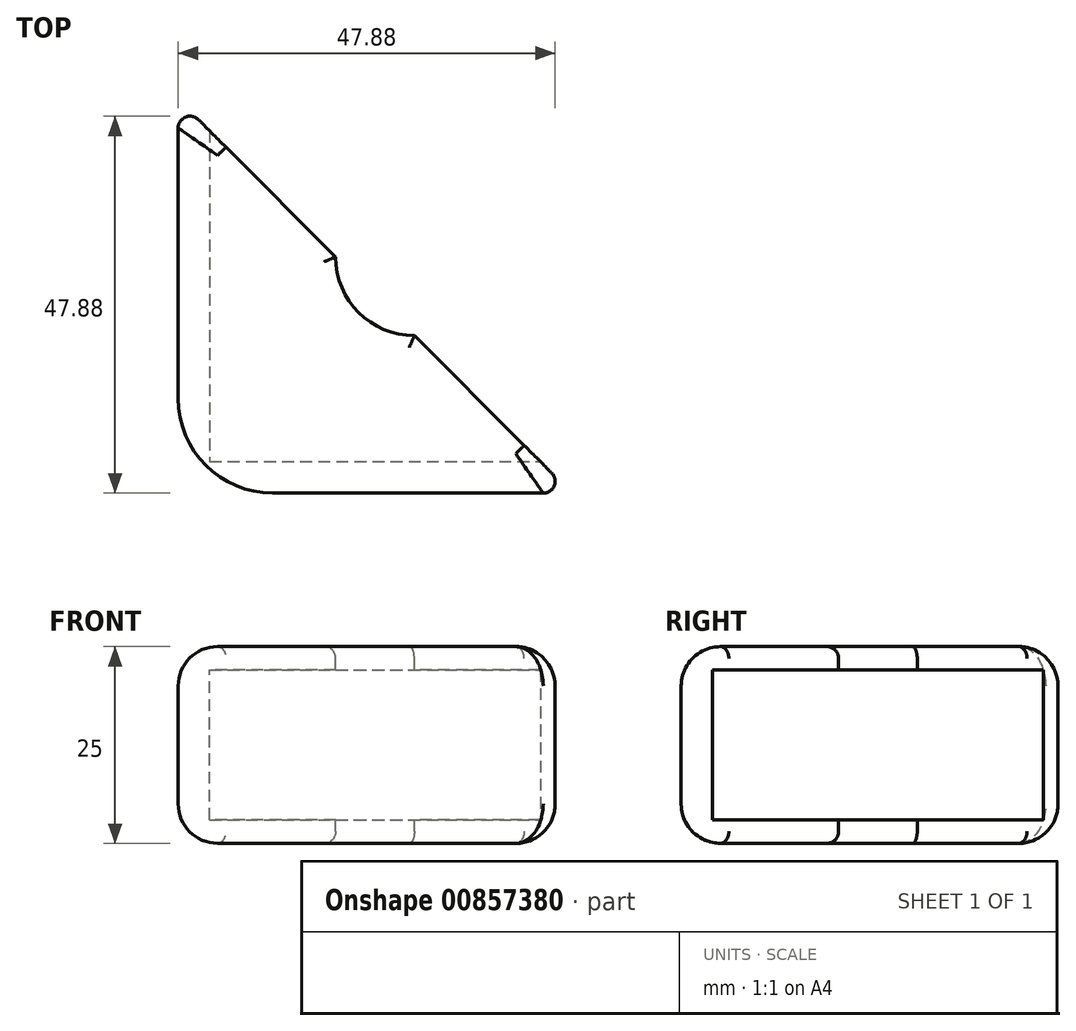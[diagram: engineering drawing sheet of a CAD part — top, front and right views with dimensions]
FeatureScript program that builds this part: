
annotation { "Feature Type Name" : "Feature", "Feature Type Description" : "" }
export const myFeature = defineFeature(function(context is Context, id is Id, definition is map)
    precondition{}
    {
        {
            var Q0;
            Q0=qCreatedBy(makeId("Top.planeOp"),FACE);
            var sketch = newSketch(context, id + "F0", { "sketchPlane" : qUnion([Q0])});
            skLineSegment(sketch, "E0.bottom", {"start": v(0, 0) * mm, "end": v(50, 0) * mm});
            skLineSegment(sketch, "E0.top", {"start": v(0, 50) * mm, "end": v(50, 50) * mm});
            skLineSegment(sketch, "E0.left", {"start": v(0, 0) * mm, "end": v(0, 50) * mm});
            skLineSegment(sketch, "E0.right", {"start": v(50, 0) * mm, "end": v(50, 50) * mm});
            skSolve(sketch);
        }
        {
            var Q0;
            Q0=makeQuery(id+"F0.imprint","IMPRINT",FACE,{"disambiguationData":[TD([[makeQuery(id+"F0.imprint","IMPRINT",EDGE,{"derivedFrom":sQuery(id+"F0.wireOp",EDGE,"E0.bottom")}),1.0]])]});
            extrude(context, id + "F1", {"entities" : qUnion([Q0]), "depth" : 25 * mm, "offsetDistance" : 25 * mm});
        }
        {
            var Q0;
            Q0=makeQuery(id+"F1.opExtrude","CAP_FACE",FACE,{"disambiguationData":[OSD([sQuery(id+"F0.wireOp",EDGE,"E0.bottom"),sQuery(id+"F0.wireOp",EDGE,"E0.top"),sQuery(id+"F0.wireOp",EDGE,"E0.left"),sQuery(id+"F0.wireOp",EDGE,"E0.right")])],"isStart":false});
            var sketch = newSketch(context, id + "F2", { "sketchPlane" : qUnion([Q0])});
            skLineSegment(sketch, "E1", {"start": v(0, 50) * mm, "end": v(50, 0) * mm});
            skLineSegment(sketch, "E2", {"start": v(50, 0) * mm, "end": v(50, 50) * mm});
            skLineSegment(sketch, "E3", {"start": v(50, 50) * mm, "end": v(0, 50) * mm});
            skSolve(sketch);
        }
        {
            var Q0;
            Q0=makeQuery(id+"F2.imprint","IMPRINT",FACE,{"disambiguationData":[TD([[makeQuery(id+"F2.imprint","IMPRINT",EDGE,{"derivedFrom":sQuery(id+"F2.wireOp",EDGE,"E1")}),1.0]])]});
            var Q1;
            Q1=makeQuery(id+"F1.opExtrude","CAP_FACE",FACE,{"disambiguationData":[OSD([sQuery(id+"F0.wireOp",EDGE,"E0.bottom"),sQuery(id+"F0.wireOp",EDGE,"E0.top"),sQuery(id+"F0.wireOp",EDGE,"E0.left"),sQuery(id+"F0.wireOp",EDGE,"E0.right")])],"isStart":true});
            extrude(context, id + "F3", {"entities" : qUnion([Q0]), "operationType" : NewBodyOperationType.REMOVE, "endBound" : BoundingType.UP_TO_SURFACE, "oppositeDirection" : true, "depth" : 25 * mm, "endBoundEntityFace" : qUnion([Q1]), "offsetDistance" : 25 * mm});
        }
        {
            var Q0;
            Q0=makeQuery(id+"F1.opExtrude","CAP_FACE",FACE,{"disambiguationData":[OSD([sQuery(id+"F0.wireOp",EDGE,"E0.bottom"),sQuery(id+"F0.wireOp",EDGE,"E0.top"),sQuery(id+"F0.wireOp",EDGE,"E0.left"),sQuery(id+"F0.wireOp",EDGE,"E0.right")])],"isStart":false});
            var sketch = newSketch(context, id + "F4", { "sketchPlane" : qUnion([Q0])});
            skLineSegment(sketch, "E4.bottom", {"start": v(20, 20) * mm, "end": v(30, 20) * mm});
            skLineSegment(sketch, "E4.left", {"start": v(20, 20) * mm, "end": v(20, 30) * mm});
            skLineSegment(sketch, "E5", {"start": v(20, 30) * mm, "end": v(30, 20) * mm});
            skSolve(sketch);
        }
        {
            var Q0;
            Q0=makeQuery(id+"F4.imprint","IMPRINT",FACE,{"disambiguationData":[TD([[makeQuery(id+"F4.imprint","IMPRINT",EDGE,{"derivedFrom":sQuery(id+"F4.wireOp",EDGE,"E4.bottom")}),1.0]])]});
            extrude(context, id + "F5", {"entities" : qUnion([Q0]), "operationType" : NewBodyOperationType.REMOVE, "endBound" : BoundingType.UP_TO_NEXT, "oppositeDirection" : true, "depth" : 25 * mm, "offsetDistance" : 25 * mm});
        }
        {
            var Q0;
            Q0=qCreatedBy(makeId("Top.planeOp"),FACE);
            cPlane(context, id + "F6", {"entities" : qUnion([Q0]), "cplaneType" : CPlaneType.OFFSET, "offset" : 3 * mm, "width" : 150 * mm, "height" : 150 * mm});
        }
        {
            var Q0;
            Q0=qCreatedBy(id+"F6.planeOp",FACE);
            var sketch = newSketch(context, id + "F7", { "sketchPlane" : qUnion([Q0])});
            skLineSegment(sketch, "E6.bottom", {"start": v(4, 49.38) * mm, "end": v(52.03, 49.38) * mm});
            skLineSegment(sketch, "E6.top", {"start": v(4, 4) * mm, "end": v(52.03, 4) * mm});
            skLineSegment(sketch, "E6.left", {"start": v(4, 49.38) * mm, "end": v(4, 4) * mm});
            skLineSegment(sketch, "E6.right", {"start": v(52.03, 49.38) * mm, "end": v(52.03, 4) * mm});
            skSolve(sketch);
        }
        {
            var Q0;
            Q0=makeQuery(id+"F7.imprint","IMPRINT",FACE,{"disambiguationData":[TD([[makeQuery(id+"F7.imprint","IMPRINT",EDGE,{"derivedFrom":sQuery(id+"F7.wireOp",EDGE,"E6.bottom")}),-1.0]])]});
            extrude(context, id + "F8", {"entities" : qUnion([Q0]), "operationType" : NewBodyOperationType.REMOVE, "depth" : 19 * mm, "offsetDistance" : 25 * mm});
        }
        {
            var Q0;
            Q0=makeQuery(id+"F1.opExtrude","SWEPT_EDGE",EDGE,{"disambiguationData":[OSD([sQuery(id+"F0.wireOp",EDGE,"E0.bottom"),sQuery(id+"F0.wireOp",EDGE,"E0.left")])]});
            fillet(context, id + "F9", {"entities" : qUnion([Q0]), "radius" : 12 * mm, "tangentPropagation" : true, "allowEdgeOverflow" : false});
        }
        {
            var Q0;
            Q0=makeQuery(id+"F1.opExtrude","CAP_EDGE",EDGE,{"disambiguationData":[OSD([sQuery(id+"F0.wireOp",EDGE,"E0.left")])],"isStart":false});
            var Q1;
            Q1=makeQuery(id+"F1.opExtrude","CAP_EDGE",EDGE,{"disambiguationData":[OSD([sQuery(id+"F0.wireOp",EDGE,"E0.left")])],"isStart":true});
            fillet(context, id + "F10", {"entities" : qUnion([Q0, Q1]), "radius" : 5 * mm, "tangentPropagation" : true, "allowEdgeOverflow" : false});
        }
        {
            var Q0;
            {var subQ0=sQuery(id+"F4.wireOp",EDGE,"E4.bottom");var subQ1=sQuery(id+"F4.wireOp",EDGE,"E4.left");Q0=makeQuery(id+"F8.boolean.opBoolean","SPLIT",EDGE,{"disambiguationData":[TD([makeQuery(id+"F1.opExtrude","CAP_FACE",FACE,{"disambiguationData":[OSD([sQuery(id+"F0.wireOp",EDGE,"E0.bottom"),sQuery(id+"F0.wireOp",EDGE,"E0.top"),sQuery(id+"F0.wireOp",EDGE,"E0.left"),sQuery(id+"F0.wireOp",EDGE,"E0.right")])],"isStart":false})])],"derivedFrom":makeQuery(id+"F5.boolean.opBoolean","COPY",EDGE,{"derivedFrom":makeQuery(id+"F5.opExtrude","SWEPT_EDGE",EDGE,{"disambiguationData":[OSD([subQ0,subQ1])]})})});}
            var Q1;
            {var subQ0=sQuery(id+"F4.wireOp",EDGE,"E4.bottom");var subQ1=sQuery(id+"F4.wireOp",EDGE,"E4.left");Q1=makeQuery(id+"F8.boolean.opBoolean","SPLIT",EDGE,{"disambiguationData":[TD([makeQuery(id+"F1.opExtrude","CAP_FACE",FACE,{"disambiguationData":[OSD([sQuery(id+"F0.wireOp",EDGE,"E0.bottom"),sQuery(id+"F0.wireOp",EDGE,"E0.top"),sQuery(id+"F0.wireOp",EDGE,"E0.left"),sQuery(id+"F0.wireOp",EDGE,"E0.right")])],"isStart":true})])],"derivedFrom":makeQuery(id+"F5.boolean.opBoolean","COPY",EDGE,{"derivedFrom":makeQuery(id+"F5.opExtrude","SWEPT_EDGE",EDGE,{"disambiguationData":[OSD([subQ0,subQ1])]})})});}
            fillet(context, id + "F11", {"entities" : qUnion([Q0, Q1]), "radius" : 10 * mm, "tangentPropagation" : true, "allowEdgeOverflow" : false});
        }
        {
            var Q0;
            {var subQ0=sQuery(id+"F0.wireOp",EDGE,"E0.bottom");Q0=makeQuery(id+"F3.boolean.opBoolean","MERGE",EDGE,{"derivedFrom":[makeQuery(id+"F1.opExtrude","SWEPT_EDGE",EDGE,{"disambiguationData":[OSD([subQ0,sQuery(id+"F0.wireOp",EDGE,"E0.right")])]}),makeQuery(id+"F3.opExtrude","SWEPT_EDGE",EDGE,{"disambiguationData":[OSD([subQ0,sQuery(id+"F2.wireOp",EDGE,"E1"),sQuery(id+"F2.wireOp",EDGE,"E2")])]})]});}
            var Q1;
            {var subQ0=sQuery(id+"F0.wireOp",EDGE,"E0.left");Q1=makeQuery(id+"F3.boolean.opBoolean","MERGE",EDGE,{"derivedFrom":[makeQuery(id+"F1.opExtrude","SWEPT_EDGE",EDGE,{"disambiguationData":[OSD([sQuery(id+"F0.wireOp",EDGE,"E0.top"),subQ0])]}),makeQuery(id+"F3.opExtrude","SWEPT_EDGE",EDGE,{"disambiguationData":[OSD([subQ0,sQuery(id+"F2.wireOp",EDGE,"E1"),sQuery(id+"F2.wireOp",EDGE,"E3")])]})]});}
            var Q2;
            {var subQ0=makeQuery(id+"F1.opExtrude","CAP_FACE",FACE,{"disambiguationData":[OSD([sQuery(id+"F0.wireOp",EDGE,"E0.bottom"),sQuery(id+"F0.wireOp",EDGE,"E0.top"),sQuery(id+"F0.wireOp",EDGE,"E0.left"),sQuery(id+"F0.wireOp",EDGE,"E0.right")])],"isStart":false});var subQ1=sQuery(id+"F4.wireOp",EDGE,"E4.bottom");var subQ2=sQuery(id+"F4.wireOp",EDGE,"E4.left");Q2=makeQuery(id+"F11.opFillet","BLEND_EDGE",EDGE,{"blendedFrom":[makeQuery(id+"F8.boolean.opBoolean","SPLIT",EDGE,{"disambiguationData":[TD([subQ0])],"derivedFrom":makeQuery(id+"F5.boolean.opBoolean","COPY",EDGE,{"derivedFrom":makeQuery(id+"F5.opExtrude","SWEPT_EDGE",EDGE,{"disambiguationData":[OSD([subQ1,subQ2])]})})}),subQ0],"blendedInto":[subQ0]});}
            var Q3;
            {var subQ0=makeQuery(id+"F1.opExtrude","CAP_FACE",FACE,{"disambiguationData":[OSD([sQuery(id+"F0.wireOp",EDGE,"E0.bottom"),sQuery(id+"F0.wireOp",EDGE,"E0.top"),sQuery(id+"F0.wireOp",EDGE,"E0.left"),sQuery(id+"F0.wireOp",EDGE,"E0.right")])],"isStart":true});var subQ1=sQuery(id+"F4.wireOp",EDGE,"E4.bottom");var subQ2=sQuery(id+"F4.wireOp",EDGE,"E4.left");Q3=makeQuery(id+"F11.opFillet","BLEND_EDGE",EDGE,{"blendedFrom":[makeQuery(id+"F8.boolean.opBoolean","SPLIT",EDGE,{"disambiguationData":[TD([subQ0])],"derivedFrom":makeQuery(id+"F5.boolean.opBoolean","COPY",EDGE,{"derivedFrom":makeQuery(id+"F5.opExtrude","SWEPT_EDGE",EDGE,{"disambiguationData":[OSD([subQ1,subQ2])]})})}),subQ0],"blendedInto":[subQ0]});}
            fillet(context, id + "F12", {"entities" : qUnion([Q0, Q1, Q2, Q3]), "radius" : 1.5 * mm, "tangentPropagation" : true, "allowEdgeOverflow" : false});
        }
    });
